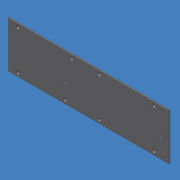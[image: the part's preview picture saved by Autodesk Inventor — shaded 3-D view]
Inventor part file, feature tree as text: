
AUTODESK INVENTOR PART (.ipt)
format: ipt  version: unknown  size: 222,720 bytes
history: native  units: mm (DEFAULTED — no unit token found)
features: sketch x4, extrude x2, hole x2
ambient origin geometry x8: Origin, YZ Plane, XZ Plane, XY Plane, X Axis, Y Axis, Z Axis, Center Point
feature tree (8):
  extrude  "Extrusion1"  Depth=79.4258mm
  extrude  "Extrusion2"  Depth=16.3068mm
  hole  "Hole1"  [1 undecoded]
  hole  "Hole2"  [1 undecoded]
  sketch  "Sketch1"  dims[d0=277.622mm d1=79.4258mm]
  sketch  "Sketch2"  dims[d2=2.2098mm d3=0.0mm d4=16.3068mm]
  sketch  "Sketch3"  dims[d5=5.7912mm d6=5.7912mm]
  sketch  "Sketch4"  dims[d7=26.2382mm d8=120.7262mm d9=168.3004mm d10=179.7812mm d11=6.6802mm d12=4.5974mm d13=0.0mm d14=3.1496mm d15=12.7mm d16=6.731mm d17=6.35mm d18=14.3117mm d19=19.05mm d20=20.594885mm d21=47.371mm d22=14.6812mm d23=165.1mm d24=5.2324mm d25=12.7mm d26=6.731mm d27=6.35mm d28=14.3117mm d29=19.05mm d30=20.594885mm]
note: 2 required parameter values undecoded (feature->parameter linkage not recoverable at this tier; creation-order binding heuristic only, values carry confidence <= 0.55)
